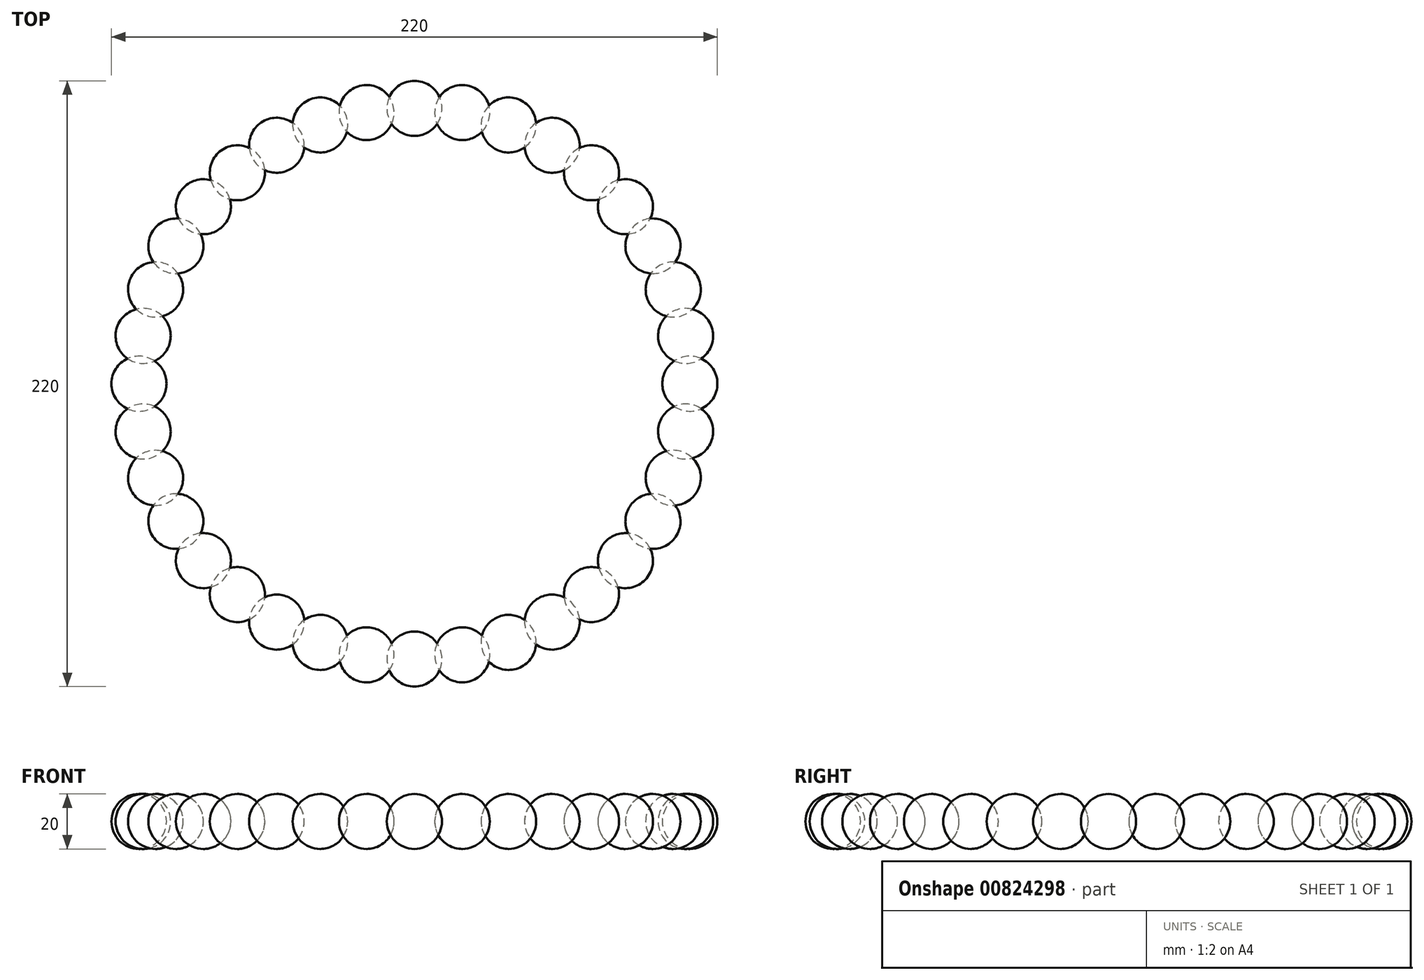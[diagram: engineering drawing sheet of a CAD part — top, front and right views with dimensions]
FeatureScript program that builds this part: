
annotation { "Feature Type Name" : "Feature", "Feature Type Description" : "" }
export const myFeature = defineFeature(function(context is Context, id is Id, definition is map)
    precondition{}
    {
        {
            var Q0;
            Q0=qCreatedBy(makeId("Front.planeOp"),FACE);
            var sketch = newSketch(context, id + "F0", { "sketchPlane" : qUnion([Q0])});
            skArc(sketch, "E0", {"start": v(100, 10) * mm, "mid": v(90, 0) * mm, "end": v(100, -10) * mm});
            skLineSegment(sketch, "E1", {"start": v(100, 10) * mm, "end": v(100, -10) * mm});
            skLineSegment(sketch, "E2", {"start": v(0, 115.87) * mm, "end": v(0, -153.8) * mm, "construction": true});
            skSolve(sketch);
        }
        {
            var Q0;
            Q0=makeQuery(id+"F0.imprint","IMPRINT",FACE,{"disambiguationData":[TD([[makeQuery(id+"F0.imprint","IMPRINT",EDGE,{"derivedFrom":sQuery(id+"F0.wireOp",EDGE,"E0")}),1.0]])]});
            var Q1;
            Q1=sQuery(id+"F0.wireOp",EDGE,"E1");
            revolve(context, id + "F1", {"surfaceOperationType" : NewSurfaceOperationType.NEW, "entities" : qUnion([Q0]), "axis" : qUnion([Q1]), "revolveType" : RevolveType.FULL});
        }
        {
            var Q0;
            Q0=makeQuery(id+"F1.opRevolve","SWEPT_BODY",BODY,{"disambiguationData":[OSD([sQuery(id+"F0.wireOp",EDGE,"E0"),sQuery(id+"F0.wireOp",EDGE,"E1")])]});
            var Q1;
            Q1=sQuery(id+"F0.wireOp",EDGE,"E2");
            circularPattern(context, id + "F2", {"entities" : qUnion([Q0]), "axis" : qUnion([Q1]), "angle" : 360 * degree, "instanceCount" : 36, "equalSpace" : true});
        }
    });
